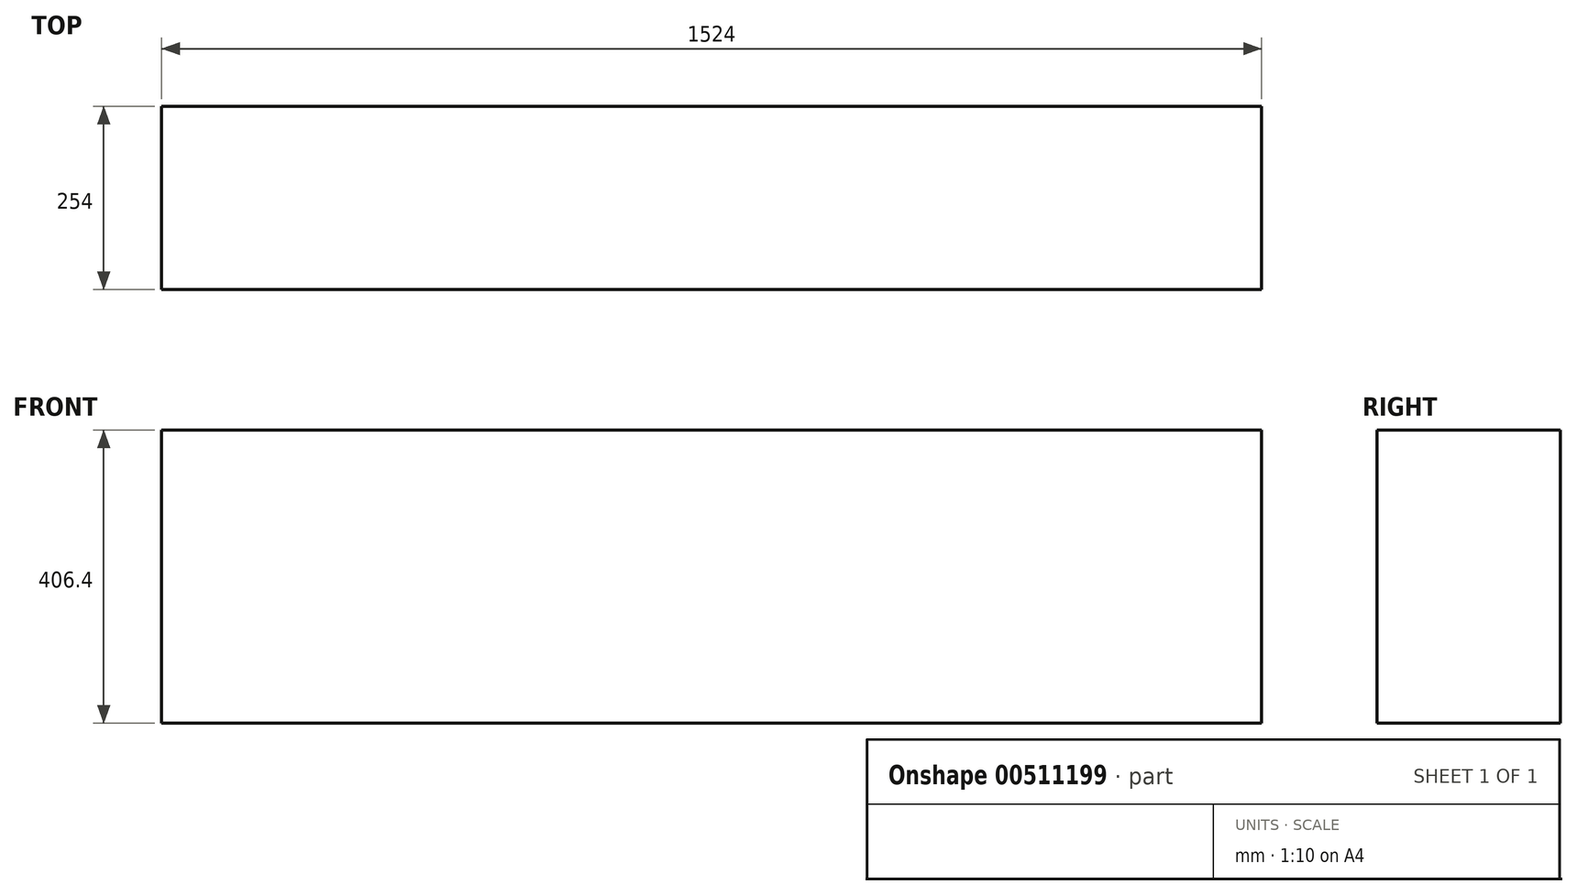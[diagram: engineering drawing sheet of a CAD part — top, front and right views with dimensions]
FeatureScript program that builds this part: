
annotation { "Feature Type Name" : "Feature", "Feature Type Description" : "" }
export const myFeature = defineFeature(function(context is Context, id is Id, definition is map)
    precondition{}
    {
        {
            var Q0;
            Q0=qCreatedBy(makeId("Front.planeOp"),FACE);
            var sketch = newSketch(context, id + "F0", { "sketchPlane" : qUnion([Q0])});
            skLineSegment(sketch, "E0.bottom", {"start": v(762, 203.2) * mm, "end": v(-762, 203.2) * mm});
            skLineSegment(sketch, "E0.top", {"start": v(762, -203.2) * mm, "end": v(-762, -203.2) * mm});
            skLineSegment(sketch, "E0.left", {"start": v(762, 203.2) * mm, "end": v(762, -203.2) * mm});
            skLineSegment(sketch, "E0.right", {"start": v(-762, 203.2) * mm, "end": v(-762, -203.2) * mm});
            skPoint(sketch, "E0.middle", {"position": v(0, 0) * mm});
            skSolve(sketch);
        }
        {
            var Q0;
            Q0 = qSketchRegion(id + "F0", true);
            extrude(context, id + "F1", {"entities" : qUnion([Q0]), "endBound" : BoundingType.SYMMETRIC, "depth" : 254 * mm});
        }
    });
